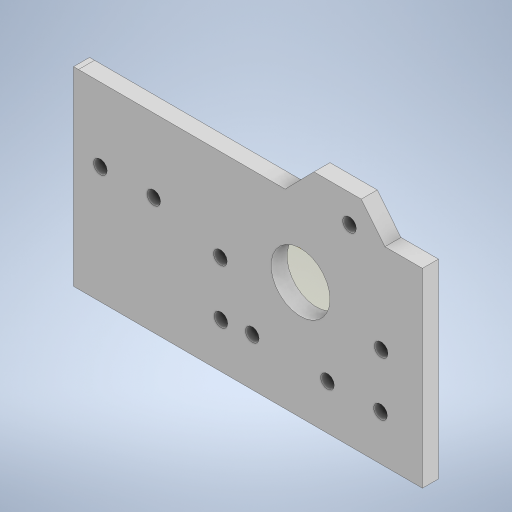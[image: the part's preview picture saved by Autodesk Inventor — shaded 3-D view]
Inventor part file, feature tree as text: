
AUTODESK INVENTOR PART (.ipt)
format: ipt  version: 2023.2 (Build 272271000, 271)  size: 430,592 bytes
history: native  units: mm
features: reference x17, other x3, sketch x2, plane x1, extrude x1, hole x1
ambient origin geometry x8: Origin, YZ Plane, XZ Plane, XY Plane, X Axis, Y Axis, Z Axis, Center Point
bodies: Solid1 (feature_tree)
feature tree (25):
  plane  "Work Plane1"
  extrude  "Extrusion1"  Depth=6.0mm
  hole  "Hole1"  [1 undecoded]
  sketch  "Sketch1"  dims[d2=110.0mm]
  reference  "Reference1"
  reference  "Reference2"
  reference  "Reference3"
  reference  "Reference4"
  reference  "Reference5"
  reference  "Reference6"
  reference  "Reference7"
  reference  "Reference8"
  reference  "Reference9"
  reference  "Reference10"
  reference  "Reference11"
  reference  "Reference12"
  reference  "Reference13"
  reference  "Reference14"
  reference  "Reference15"
  reference  "Reference16"
  reference  "Reference17"
  sketch  "Sketch2"  dims[d3=5.1mm d4=5.1mm d5=5.1mm d7=7.0mm d8=7.0mm d9=7.0mm d10=3.0mm d11=20.0mm d12=22.1mm d13=6.0mm d14=0.0mm d16=5.1mm d17=6.0mm d18=4.0mm d19=2.0mm d20=90.0deg d21=8.0mm d22=20.594885mm d30=15.0mm d33=54.0mm d36=20.0mm d37=15.000003mm]
  parser-record x1  (decoder bookkeeping rows leaked as tree rows — omitted from the tree; the rows remain in map.json)
  other  "Main Assembly.iam"
  other  "C beam extrusion 460:1"
note: 1 required parameter value undecoded (feature->parameter linkage not recoverable at this tier; creation-order binding heuristic only, values carry confidence <= 0.55)
note: 1 file-system path scrubbed to <path> (originals preserved in map.json)
